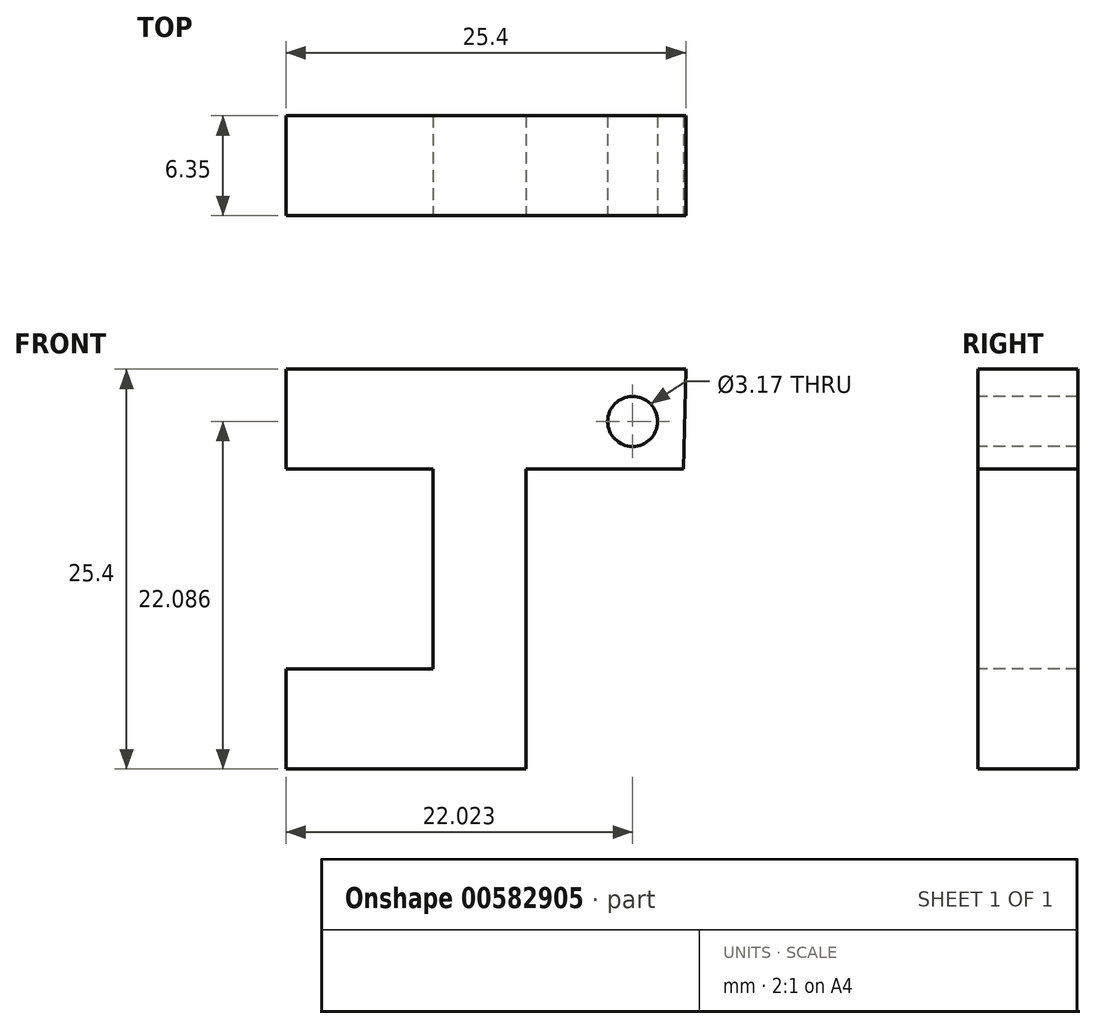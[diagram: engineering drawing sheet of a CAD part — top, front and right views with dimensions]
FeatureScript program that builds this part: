
annotation { "Feature Type Name" : "Feature", "Feature Type Description" : "" }
export const myFeature = defineFeature(function(context is Context, id is Id, definition is map)
    precondition{}
    {
        {
            var Q0;
            Q0=qCreatedBy(makeId("Front.planeOp"),FACE);
            var sketch = newSketch(context, id + "F0", { "sketchPlane" : qUnion([Q0])});
            skLineSegment(sketch, "E0", {"start": v(0, 0) * mm, "end": v(0, 25.4) * mm});
            skLineSegment(sketch, "E1", {"start": v(25.4, 25.4) * mm, "end": v(25.4, 0) * mm});
            skLineSegment(sketch, "E2", {"start": v(25.4, 0) * mm, "end": v(0, 0) * mm});
            skLineSegment(sketch, "E3", {"start": v(0, 25.4) * mm, "end": v(25.4, 25.4) * mm});
            skSolve(sketch);
        }
        {
            var Q0;
            Q0 = qSketchRegion(id + "F0", true);
            extrude(context, id + "F1", {"entities" : qUnion([Q0]), "depth" : 6.35 * mm, "offsetDistance" : 25.4 * mm});
        }
        {
            var Q0;
            Q0=makeQuery(id+"F1.opExtrude","CAP_FACE",FACE,{"disambiguationData":[OSD([sQuery(id+"F0.wireOp",EDGE,"E0"),sQuery(id+"F0.wireOp",EDGE,"E1"),sQuery(id+"F0.wireOp",EDGE,"E2"),sQuery(id+"F0.wireOp",EDGE,"E3")])],"isStart":false});
            var sketch = newSketch(context, id + "F2", { "sketchPlane" : qUnion([Q0])});
            skLineSegment(sketch, "E4", {"start": v(0, 19.05) * mm, "end": v(9.34, 19.05) * mm});
            skLineSegment(sketch, "E5", {"start": v(9.34, 19.05) * mm, "end": v(9.34, 6.35) * mm});
            skLineSegment(sketch, "E6", {"start": v(9.34, 6.35) * mm, "end": v(0, 6.35) * mm});
            skLineSegment(sketch, "E7", {"start": v(0, 6.35) * mm, "end": v(0, 0) * mm});
            skLineSegment(sketch, "E8", {"start": v(15.24, 19.05) * mm, "end": v(25.26, 19.05) * mm});
            skLineSegment(sketch, "E9", {"start": v(25.26, 19.05) * mm, "end": v(25.4, 25.4) * mm});
            skLineSegment(sketch, "E10", {"start": v(25.4, 25.4) * mm, "end": v(0, 25.4) * mm});
            skLineSegment(sketch, "E11", {"start": v(0, 25.4) * mm, "end": v(0, 19.05) * mm});
            skLineSegment(sketch, "E12", {"start": v(0, 0) * mm, "end": v(15.24, 0) * mm});
            skLineSegment(sketch, "E13", {"start": v(15.24, 0) * mm, "end": v(15.24, 19.05) * mm});
            skLineSegment(sketch, "E14", {"start": v(0, 0) * mm, "end": v(25.4, 0) * mm});
            skLineSegment(sketch, "E15", {"start": v(25.4, 0) * mm, "end": v(25.4, 25.4) * mm});
            skLineSegment(sketch, "E16", {"start": v(0, 25.4) * mm, "end": v(0, 0) * mm});
            skSolve(sketch);
        }
        {
            var Q0;
            {var subQ0=sQuery(id+"F2.wireOp",EDGE,"E4");Q0=makeQuery(id+"F2.imprint","IMPRINT",FACE,{"disambiguationData":[TD([[makeQuery(id+"F2.imprint","IMPRINT",EDGE,{"derivedFrom":subQ0}),-1.0]])]});}
            var Q1;
            Q1=makeQuery(id+"F2.imprint","IMPRINT",FACE,{"disambiguationData":[TD([[makeQuery(id+"F2.imprint","IMPRINT",EDGE,{"derivedFrom":sQuery(id+"F2.wireOp",EDGE,"E8")}),-1.0]])]});
            extrude(context, id + "F3", {"entities" : qUnion([Q0, Q1]), "operationType" : NewBodyOperationType.REMOVE, "oppositeDirection" : true, "depth" : 25.4 * mm, "offsetDistance" : 25.4 * mm});
        }
        {
            var Q0;
            Q0=makeQuery(id+"F1.opExtrude","CAP_FACE",FACE,{"disambiguationData":[OSD([sQuery(id+"F0.wireOp",EDGE,"E0"),sQuery(id+"F0.wireOp",EDGE,"E1"),sQuery(id+"F0.wireOp",EDGE,"E2"),sQuery(id+"F0.wireOp",EDGE,"E3")])],"isStart":false});
            var sketch = newSketch(context, id + "F4", { "sketchPlane" : qUnion([Q0])});
            skCircle(sketch, "E17", {"center": v(22.02, 22.09) * mm, "radius": 1.59 * mm});
            skSolve(sketch);
        }
        {
            var Q0;
            Q0=makeQuery(id+"F4.imprint","IMPRINT",FACE,{"disambiguationData":[TD([[makeQuery(id+"F4.imprint","IMPRINT",EDGE,{"derivedFrom":sQuery(id+"F4.wireOp",EDGE,"E17")}),1.0]])]});
            extrude(context, id + "F5", {"entities" : qUnion([Q0]), "operationType" : NewBodyOperationType.REMOVE, "oppositeDirection" : true, "depth" : 25.4 * mm, "offsetDistance" : 25.4 * mm});
        }
    });
